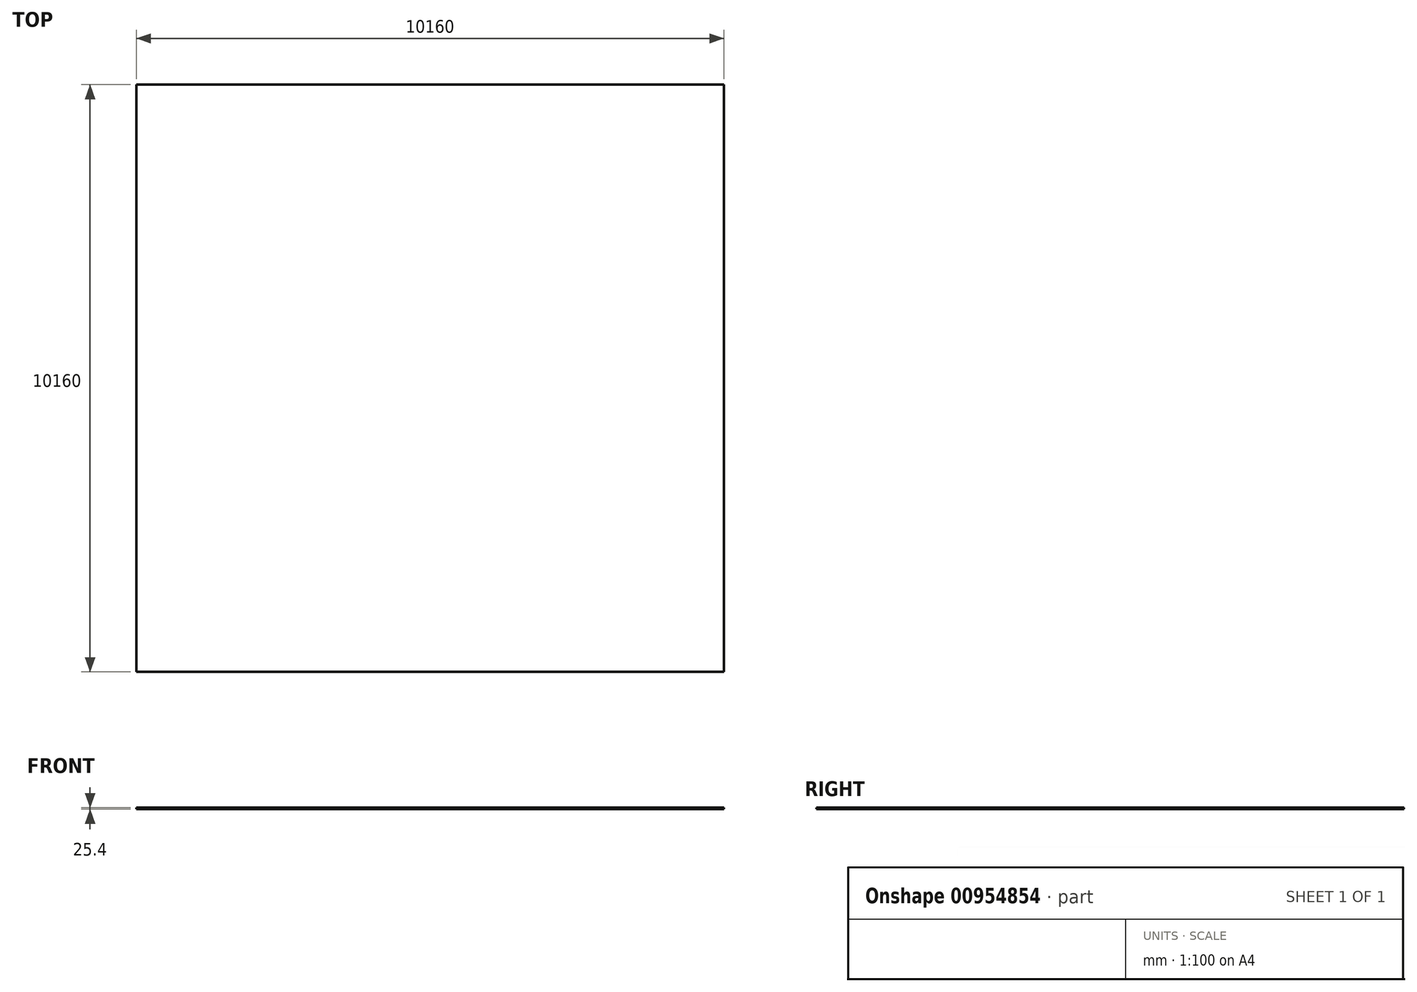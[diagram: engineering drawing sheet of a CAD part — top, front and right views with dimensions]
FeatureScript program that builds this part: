
annotation { "Feature Type Name" : "Feature", "Feature Type Description" : "" }
export const myFeature = defineFeature(function(context is Context, id is Id, definition is map)
    precondition{}
    {
        {
            var Q0;
            Q0=qCreatedBy(makeId("Front.planeOp"),FACE);
            var sketch = newSketch(context, id + "F0", { "sketchPlane" : qUnion([Q0])});
            skLineSegment(sketch, "E0.bottom", {"start": v(0, 0) * mm, "end": v(5080, 0) * mm});
            skLineSegment(sketch, "E0.top", {"start": v(0, -25.4) * mm, "end": v(5080, -25.4) * mm});
            skLineSegment(sketch, "E0.left", {"start": v(0, 0) * mm, "end": v(0, -25.4) * mm});
            skLineSegment(sketch, "E0.right", {"start": v(5080, 0) * mm, "end": v(5080, -25.4) * mm});
            skLineSegment(sketch, "E1.bottom", {"start": v(0, 0) * mm, "end": v(-5080, 0) * mm});
            skLineSegment(sketch, "E1.top", {"start": v(0, -25.4) * mm, "end": v(-5080, -25.4) * mm});
            skLineSegment(sketch, "E1.right", {"start": v(-5080, 0) * mm, "end": v(-5080, -25.4) * mm});
            skSolve(sketch);
        }
        {
            var Q0;
            Q0=makeQuery(id+"F0.imprint","IMPRINT",FACE,{"disambiguationData":[TD([[makeQuery(id+"F0.imprint","IMPRINT",EDGE,{"derivedFrom":sQuery(id+"F0.wireOp",EDGE,"E1.bottom")}),1.0]])]});
            var Q1;
            Q1=makeQuery(id+"F0.imprint","IMPRINT",FACE,{"disambiguationData":[TD([[makeQuery(id+"F0.imprint","IMPRINT",EDGE,{"derivedFrom":sQuery(id+"F0.wireOp",EDGE,"E0.bottom")}),-1.0]])]});
            extrude(context, id + "F1", {"entities" : qUnion([Q0, Q1]), "depth" : 5080 * mm, "offsetDistance" : 25.4 * mm, "hasSecondDirection" : true, "secondDirectionOppositeDirection" : true, "secondDirectionDepth" : 5080 * mm});
        }
    });
